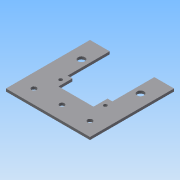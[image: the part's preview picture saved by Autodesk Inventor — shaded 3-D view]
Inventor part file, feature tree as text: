
AUTODESK INVENTOR PART (.ipt)
format: ipt  version: 2015 (Build 190159000, 159)  size: 121,856 bytes
history: native  units: in
note: dims shown in document units (in); Inventor stores cm internally (conversion verified against a paired STEP export)
features: sketch x5, hole x3, extrude x2
ambient origin geometry x8: Origin, YZ Plane, XZ Plane, XY Plane, X Axis, Y Axis, Z Axis, Center Point
bodies: Solid1 (feature_tree)
feature tree (10):
  extrude  "Extrusion1"  Depth=3.0in
  hole  "Hole1"  [1 undecoded]
  hole  "Hole2"  [1 undecoded]
  extrude  "Extrusion2"  Depth=1.25in
  hole  "Hole3"  [1 undecoded]
  sketch  "Sketch1"  dims[d0=3.0in d1=3.0in]
  sketch  "Sketch2"  dims[d2=0.0938in d3=0.0in d4=0.5in]
  sketch  "Sketch3"  dims[d5=0.5in d6=1.0in]
  sketch  "Sketch4"  dims[d7=0.177in d8=0.75in d9=0.332in d10=0.25in d11=0.5635in d12=1.0in d13=0.8108in d14=1.25in]
  sketch  "Sketch5"  dims[d16=1.595in d17=0.125in d18=0.75in d19=0.332in d20=0.25in d21=0.5635in d22=1.0in d23=0.8108in d24=1.5in d25=0.0938in d26=0.0in d27=1.25in d28=0.5in d29=1.595in d30=0.75in d31=2.11in d32=0.25in d33=0.75in d34=0.279in d35=0.25in d36=0.5635in d37=1.0in d38=0.8108in d39=1.0in]
note: 3 required parameter values undecoded (feature->parameter linkage not recoverable at this tier; creation-order binding heuristic only, values carry confidence <= 0.55)
